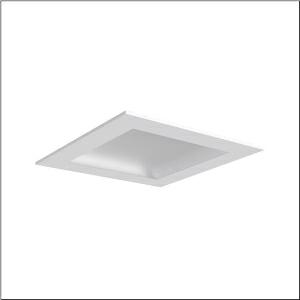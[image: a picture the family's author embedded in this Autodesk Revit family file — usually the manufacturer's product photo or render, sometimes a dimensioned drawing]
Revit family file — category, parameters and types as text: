
# Revit family: mira_r__11_sl_51fr427a443a_65dc
name_source: partatom
category: Lighting Fixtures
units: mm (PartAtom-declared; Revit-internal decimal feet)

## family parameters
Cut with Voids When Loaded = No
Host = Face
Light Source = No
Part Type = Normal
Room Calculation Point = No
Round Connector Dimension = Use Diameter
Shared = No

## types (1)
- Mira® 11 SL (1 x LED, 4430 lm, 40 W, 4000K)
    Apparent Load = 40 VA
    CIE Flux Codes = 50 81 97 100 100
    Color Rendering = 80
    Color Temperature = 4000K
    Default Elevation = 1800 mm
    Description = Mira® 11 SL, clean room luminaire, primary light control with reflector, primary optical cover: cover, of PC, light emission: direct distribution, primary light characteristic: symmetric, installation type: recessed, LED, rated luminous flux: 4.430lm, luminous efficacy: 111lm/W, light colour: 840, colour temperature: 4000K, control gear: ECG, with terminal, 3-pole, max. 2.5mm², mains connection: 230V, AC, 50/60Hz, rated input power: 40W, luminaire housing, of sheet steel, coated, pure white (RAL 9010), with wing nuts, module: M625, length: 623mm, width: 623mm, height: 91mm, protection rating (complete): IP54, protection rating (on room side): IP65, insulation class (complete): insulation class I (protective earthing), certification: CE, UKCA, permissible operating ambient temperature: -5..+40°C, standard: EN 50419, packaging unit: 1 piece
    Height = 0 mm  [stored 0 ft]
    Lamp = 1 x LED
    Lamp Light Flux = 4430 lm
    Lamp Power = 40 W
    Lamp count = 1
    Length = 625 mm
    Luminous efficacy = 111 lm/W
    Manufacturer = Siteco
    ModVariant = No
    Model = 51FR427A443A
    Mounting Place = Ceiling
    Mounting Type = Recessed
    Number of Poles = 1
    OnlyDefault = Yes
    Power Factor = 1
    Product Name = Mira® 11 SL
    Product group = clean room luminaire
    ProductGroupID = 402
    Protection Class = Protection class I
    Protection Degree = IP 54
    RLX_Detail_Level = 1
    RLX_Emergency_Light_Flux = 0 lm
    RLX_Emergency_Type = 0
    RLX_Emergency_Type_DB = No
    RlxData = <blob elided: 19917 chars, md5=fb4f318f>
    Socket = socket
    Standby Power = 0 W
    System Light Flux = 4430 lm
    System Power = 40 W
    Type Comments = Product without accessories
    Type Image = l_1007111.jpg
    URL = http://relux.com
    VarID = ---
    Voltage = 0 V
    Weight = 0.00 kg
    Width = 625 mm

note: [stored X ft] marks values corroborated as IEEE doubles in the binary element streams (Revit-internal decimal feet)

## geometry (parser evidence)
native form markers: Blend x4, Sweep x11
no freeform markers — native parametric forms only
